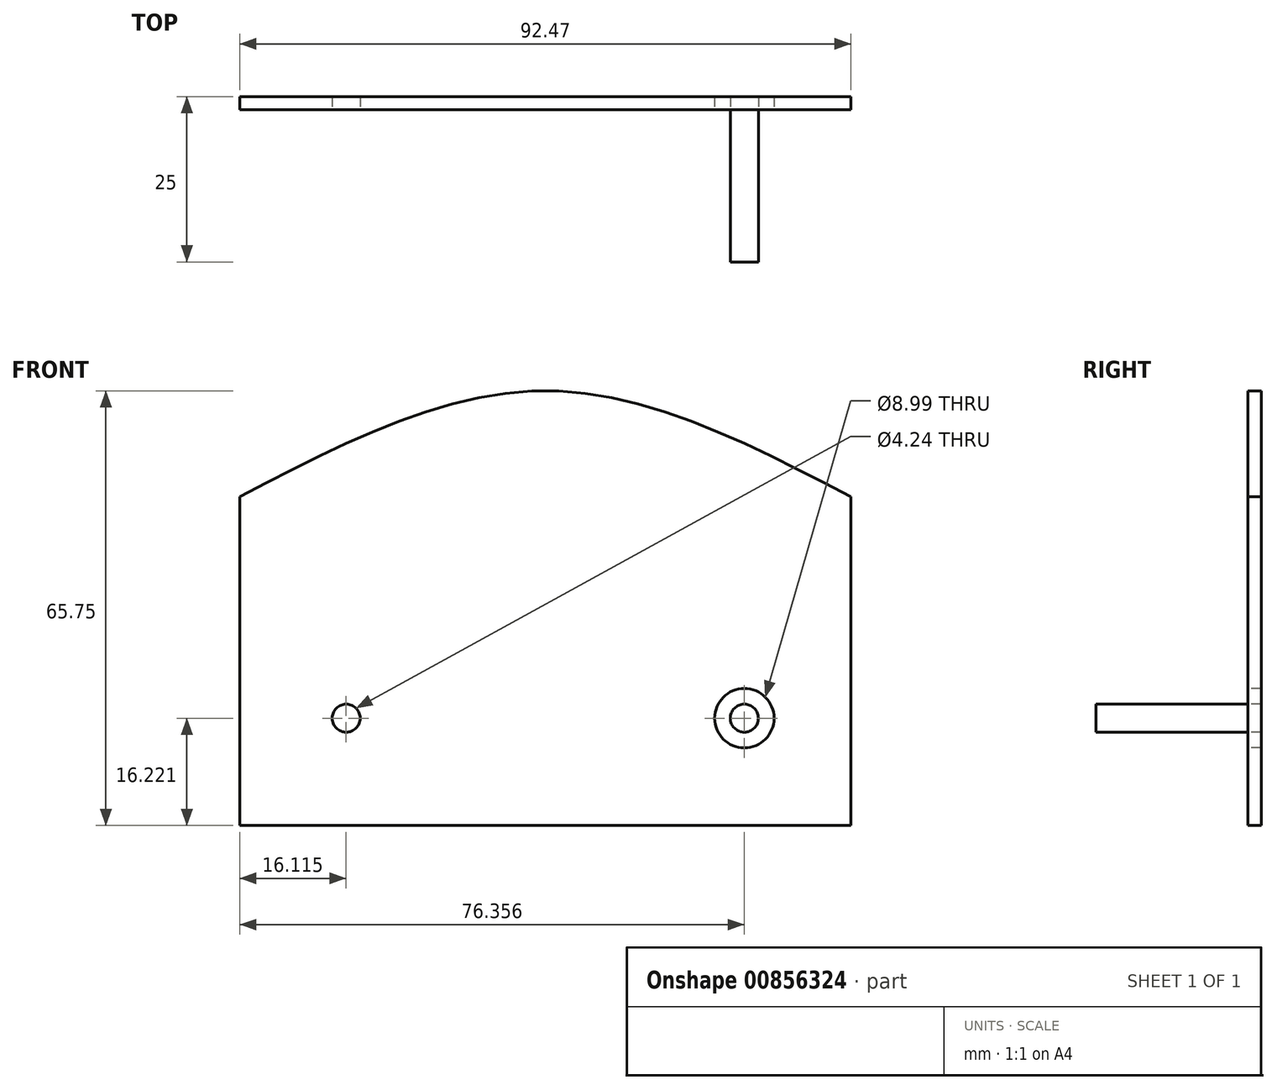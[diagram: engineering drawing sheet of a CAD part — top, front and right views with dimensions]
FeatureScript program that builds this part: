
annotation { "Feature Type Name" : "Feature", "Feature Type Description" : "" }
export const myFeature = defineFeature(function(context is Context, id is Id, definition is map)
    precondition{}
    {
        {
            var Q0;
            Q0=qCreatedBy(makeId("Front.planeOp"),FACE);
            var sketch = newSketch(context, id + "F0", { "sketchPlane" : qUnion([Q0])});
            skLineSegment(sketch, "E0.bottom", {"start": v(0, 0) * mm, "end": v(92.47, 0) * mm});
            skLineSegment(sketch, "E0.top", {"start": v(0, 49.76) * mm, "end": v(92.47, 49.76) * mm});
            skLineSegment(sketch, "E0.left", {"start": v(0, 0) * mm, "end": v(0, 49.76) * mm});
            skLineSegment(sketch, "E0.right", {"start": v(92.47, 0) * mm, "end": v(92.47, 49.76) * mm});
            skPoint(sketch, "E1.1.internal.snap0", {"position": v(46.24, 49.76) * mm});
            skFitSpline(sketch, "E1", {"points": [v(0, 49.76) * mm, v(46.24, 65.75) * mm, v(92.47, 49.76) * mm], "startDerivative": vector(92.47, 47.98) * mm, "endDerivative": vector(92.47, -47.98) * mm});
            skSolve(sketch);
        }
        {
            var Q0;
            Q0=makeQuery(id+"F0.imprint","IMPRINT",FACE,{"disambiguationData":[TD([[makeQuery(id+"F0.imprint","IMPRINT",EDGE,{"derivedFrom":sQuery(id+"F0.wireOp",EDGE,"E0.top")}),1.0]])]});
            var Q1;
            Q1=makeQuery(id+"F0.imprint","IMPRINT",FACE,{"disambiguationData":[TD([[makeQuery(id+"F0.imprint","IMPRINT",EDGE,{"derivedFrom":sQuery(id+"F0.wireOp",EDGE,"E0.bottom")}),1.0]])]});
            extrude(context, id + "F1", {"entities" : qUnion([Q0, Q1]), "depth" : 25 * mm, "offsetDistance" : 25 * mm});
        }
        {
            var Q0;
            Q0=makeQuery(id+"F1.opExtrude","CAP_FACE",FACE,{"disambiguationData":[OSD([sQuery(id+"F0.wireOp",EDGE,"E0.bottom"),sQuery(id+"F0.wireOp",EDGE,"E0.left"),sQuery(id+"F0.wireOp",EDGE,"E0.right"),sQuery(id+"F0.wireOp",EDGE,"E1")])],"isStart":false});
            var sketch = newSketch(context, id + "F2", { "sketchPlane" : qUnion([Q0])});
            skFitSpline(sketch, "E2.0", {"points": [v(-3.22, 55.97) * mm, v(0.63, 57.97) * mm, v(6.49, 61.01) * mm, v(14.47, 64.77) * mm, v(20.56, 67.34) * mm, v(26.76, 69.55) * mm, v(32.05, 71.01) * mm, v(36.34, 71.88) * mm, v(39.6, 72.37) * mm, v(42.35, 72.63) * mm, v(44.57, 72.73) * mm, v(46.24, 72.76) * mm, v(47.9, 72.73) * mm, v(50.12, 72.63) * mm, v(52.87, 72.37) * mm, v(56.13, 71.88) * mm, v(60.42, 71.01) * mm, v(65.7, 69.55) * mm, v(71.91, 67.34) * mm, v(78, 64.77) * mm, v(85.98, 61.01) * mm, v(91.84, 57.97) * mm, v(95.7, 55.97) * mm]});
            skLineSegment(sketch, "E3", {"start": v(0, 49.76) * mm, "end": v(0, 57.64) * mm});
            skLineSegment(sketch, "E4", {"start": v(92.47, 49.76) * mm, "end": v(92.47, 57.64) * mm});
            skSolve(sketch);
        }
        {
            var Q0;
            Q0 = qSketchRegion(id + "F2", true);
            var Q1;
            Q1=makeQuery(id+"F2.imprint","IMPRINT",FACE,{"disambiguationData":[TD([[makeQuery(id+"F2.imprint","IMPRINT",EDGE,{"derivedFrom":sQuery(id+"F2.wireOp",EDGE,"E2.0")}),-1.0]])]});
            extrude(context, id + "F3", {"entities" : qUnion([Q0, Q1]), "operationType" : NewBodyOperationType.ADD, "oppositeDirection" : true, "depth" : 5 * mm, "offsetDistance" : 25 * mm});
        }
        {
            var Q0;
            {var subQ0=sQuery(id+"F0.wireOp",EDGE,"E1");Q0=makeQuery(id+"F3.boolean.opBoolean","MERGE",FACE,{"derivedFrom":[makeQuery(id+"F1.opExtrude","CAP_FACE",FACE,{"disambiguationData":[OSD([sQuery(id+"F0.wireOp",EDGE,"E0.bottom"),sQuery(id+"F0.wireOp",EDGE,"E0.left"),sQuery(id+"F0.wireOp",EDGE,"E0.right"),subQ0])],"isStart":false}),makeQuery(id+"F3.opExtrude","CAP_FACE",FACE,{"disambiguationData":[OSD([subQ0,sQuery(id+"F2.wireOp",EDGE,"E2.0"),sQuery(id+"F2.wireOp",EDGE,"E3"),sQuery(id+"F2.wireOp",EDGE,"E4")])],"isStart":true})]});}
            var sketch = newSketch(context, id + "F4", { "sketchPlane" : qUnion([Q0])});
            skCircle(sketch, "E5", {"center": v(16.12, 16.22) * mm, "radius": 4.5 * mm});
            skCircle(sketch, "E6", {"center": v(16.12, 16.22) * mm, "radius": 2.12 * mm});
            skLineSegment(sketch, "E7", {"start": v(46.24, 0) * mm, "end": v(46.24, 72.75) * mm});
            skCircle(sketch, "E8.MirrorC", {"center": v(76.36, 16.22) * mm, "radius": 4.5 * mm});
            skCircle(sketch, "E9.MirrorC", {"center": v(76.36, 16.22) * mm, "radius": 2.12 * mm});
            skSolve(sketch);
        }
        {
            var Q0;
            Q0=makeQuery(id+"F4.imprint","IMPRINT",FACE,{"disambiguationData":[TD([[makeQuery(id+"F4.imprint","IMPRINT",EDGE,{"derivedFrom":sQuery(id+"F4.wireOp",EDGE,"E5")}),1.0]])]});
            var Q1;
            Q1=makeQuery(id+"F4.imprint","IMPRINT",FACE,{"disambiguationData":[TD([[makeQuery(id+"F4.imprint","IMPRINT",EDGE,{"derivedFrom":sQuery(id+"F4.wireOp",EDGE,"E6")}),1.0]])]});
            var Q2;
            Q2=makeQuery(id+"F4.imprint","IMPRINT",FACE,{"disambiguationData":[TD([[makeQuery(id+"F4.imprint","IMPRINT",EDGE,{"derivedFrom":sQuery(id+"F4.wireOp",EDGE,"E8.MirrorC")}),-1.0]])]});
            var Q3;
            Q3=makeQuery(id+"F4.imprint","IMPRINT",FACE,{"disambiguationData":[TD([[makeQuery(id+"F4.imprint","IMPRINT",EDGE,{"derivedFrom":sQuery(id+"F4.wireOp",EDGE,"E9.MirrorC")}),-1.0]])]});
            extrude(context, id + "F5", {"entities" : qUnion([Q0, Q1, Q2, Q3]), "operationType" : NewBodyOperationType.REMOVE, "oppositeDirection" : true, "depth" : 23 * mm, "offsetDistance" : 25 * mm});
        }
        {
            var Q0;
            Q0=makeQuery(id+"F4.imprint","IMPRINT",FACE,{"disambiguationData":[TD([[makeQuery(id+"F4.imprint","IMPRINT",EDGE,{"derivedFrom":sQuery(id+"F4.wireOp",EDGE,"E6")}),1.0]])]});
            var Q1;
            Q1=makeQuery(id+"F4.imprint","IMPRINT",FACE,{"disambiguationData":[TD([[makeQuery(id+"F4.imprint","IMPRINT",EDGE,{"derivedFrom":sQuery(id+"F4.wireOp",EDGE,"E9.MirrorC")}),-1.0]])]});
            extrude(context, id + "F6", {"entities" : qUnion([Q0, Q1]), "operationType" : NewBodyOperationType.REMOVE, "oppositeDirection" : true, "depth" : 25 * mm, "offsetDistance" : 25 * mm});
        }
    });
